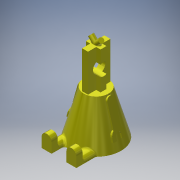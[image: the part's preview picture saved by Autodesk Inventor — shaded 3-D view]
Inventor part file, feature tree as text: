
AUTODESK INVENTOR PART (.ipt)
format: ipt  version: 2019 (Build 230136000, 136)  size: 391,168 bytes
history: native  units: mm
features: sketch x9, other x6, extrude x6, revolve x2, mirror x2, fillet x2, reference x1, projected_geometry x1
ambient origin geometry x8: Origin, YZ Plane, XZ Plane, XY Plane, X Axis, Y Axis, Z Axis, Center Point
bodies: Body1 (feature_tree)
feature tree (29):
  other  "ソリッド1"
  revolve  "回転1"
  extrude  "押し出し1"  TaperAngle=90.0deg  [1 undecoded]
  extrude  "足"  Depth=35.0mm
  sketch  "スケッチ7"
  other  "作業平面3"
  extrude  "腕"  Depth=20.0mm
  mirror  "ミラー1"
  sketch  "スケッチ9"
  other  "作業平面4"
  extrude  "押し出し4"  Depth=10.0mm
  extrude  "押し出し5"  Depth=25.0mm TaperAngle=0.0deg
  revolve  "回転2"
  mirror  "ミラー3"
  fillet  "フィレット1"  Radius=10.0mm
  fillet  "フィレット2"  Radius=4.0mm
  extrude  "押し出し6"  Depth=8.0mm
  sketch  "スケッチ1"
  sketch  "スケッチ5"
  sketch  "スケッチ6"
  sketch  "スケッチ8"
  sketch  "スケッチ10"
  reference  "参照1"
  sketch  "スケッチ11"
  sketch  "スケッチ12"
  projected_geometry  "投影ループ4"
  other  "<userpath>\OneDrive\デスクトップ\mini_robot\mini_robot.iam"
  other  "mini_robot.iam"
  other  "head:1"
note: 1 required parameter value undecoded (feature->parameter linkage not recoverable at this tier; creation-order binding heuristic only, values carry confidence <= 0.55)
